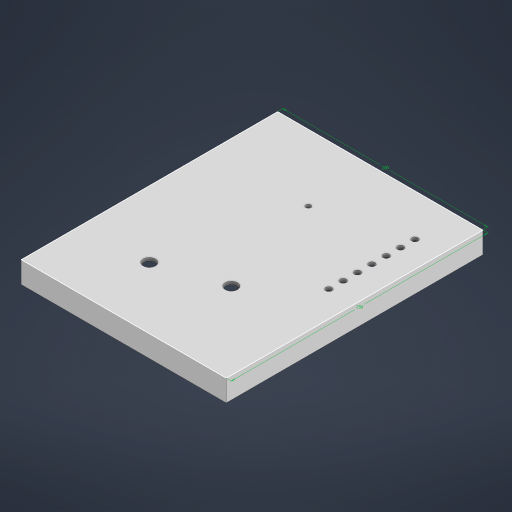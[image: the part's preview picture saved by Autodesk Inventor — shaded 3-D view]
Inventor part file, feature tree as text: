
AUTODESK INVENTOR PART (.ipt)
format: ipt  version: 2023 (Build 270158000, 158)  size: 223,232 bytes
history: native  units: mm
features: extrude x4, other x2, sketch x2, shell x1, plane x1
ambient origin geometry x8: Origin, YZ Plane, XZ Plane, XY Plane, X Axis, Y Axis, Z Axis, Center Point
bodies: Body1 (feature_tree)
feature tree (10):
  other  "block"
  extrude  "ext_block"  Depth=250.0mm
  shell  "Shell2"  Thickness=12.0mm
  extrude  "holes"  Depth=12.0mm
  extrude  "pwr_button_hole"  Depth=17.0mm
  plane  "Work Plane1"
  extrude  "back_cover_cut"  Depth=17.0mm
  other  "lines_base"
  sketch  "Sketch4"  dims[d0=200.0mm d1=250.0mm d2=12.0mm]
  sketch  "Sketch5"  dims[d3=12.0mm d4=25.0mm d5=17.0mm d6=17.0mm d7=25.0mm d8=75.0mm d9=80.0mm d10=65.0mm d11=60.0mm d12=6.0mm d13=84.0mm d14=90.0deg d15=25.0mm d16=125.0mm d17=70.0mm d19=14.0mm d20=10.0mm d22=10.0mm d24=5.0mm d25=10.0mm d26=65.0mm d27=95.0mm d31=200.0mm d32=250.0mm d35=24.0mm d36=0.0mm d37=3.0mm d38=24.0mm d39=0.0mm d40=19.0mm d41=13.0mm d42=4.0mm d43=12.0mm d44=24.0mm d45=0.0mm d49=0.0mm d50=0.0mm d33=0.5mm d34=0.872665mm d62=0.5mm d63=0.872665mm d64=0.5mm d65=0.872665mm]
